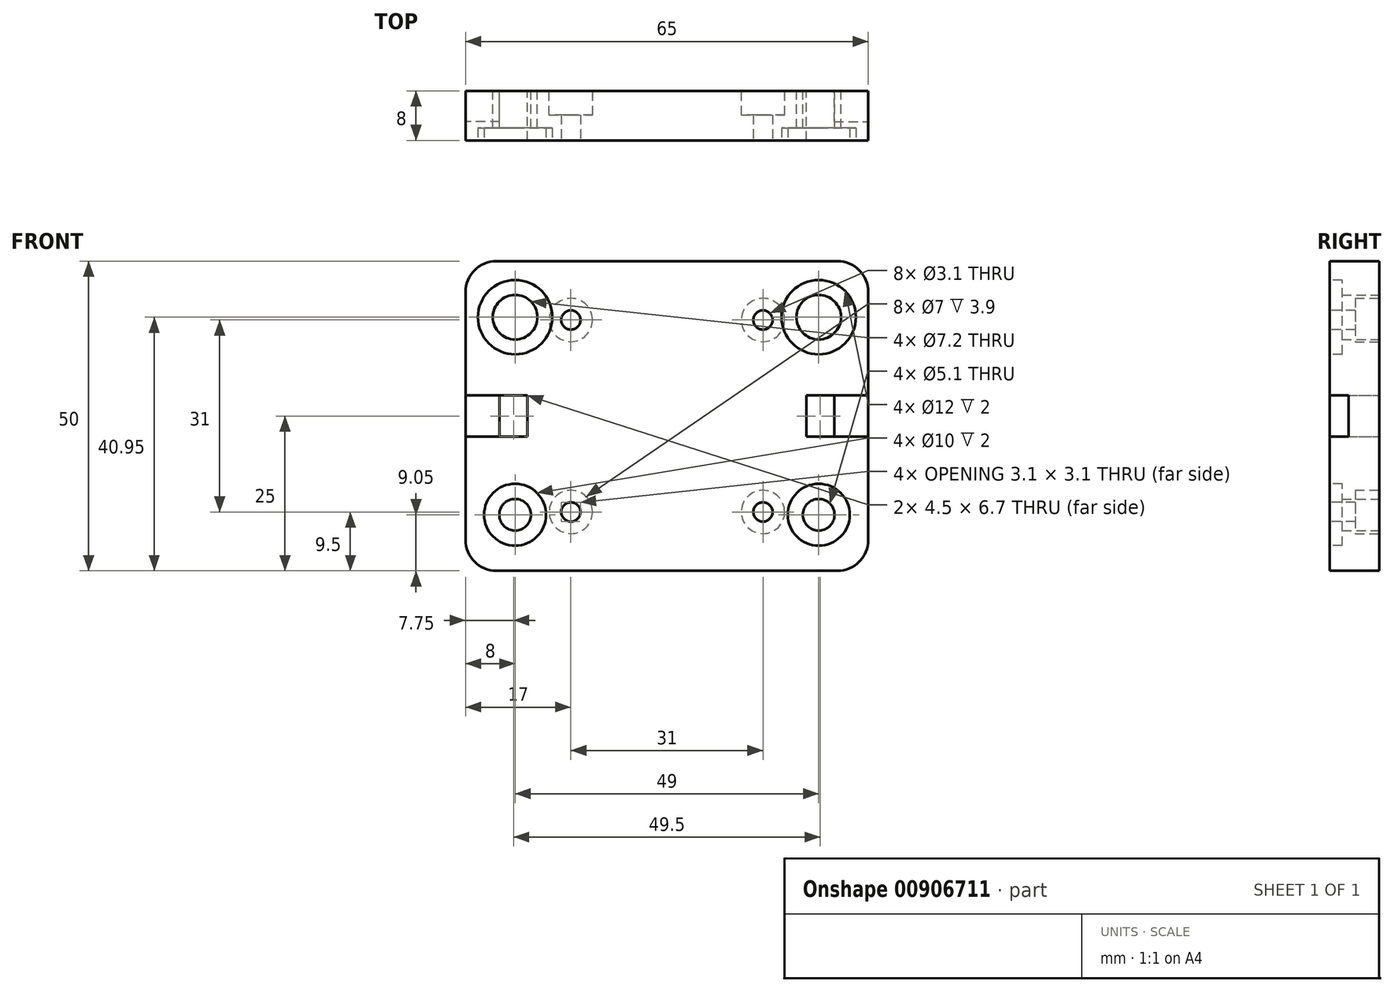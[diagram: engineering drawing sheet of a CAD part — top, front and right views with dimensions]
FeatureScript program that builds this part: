
annotation { "Feature Type Name" : "Feature", "Feature Type Description" : "" }
export const myFeature = defineFeature(function(context is Context, id is Id, definition is map)
    precondition{}
    {
        {
            var Q0;
            Q0=qCreatedBy(makeId("Front.planeOp"),FACE);
            var sketch = newSketch(context, id + "F0", { "sketchPlane" : qUnion([Q0])});
            skLineSegment(sketch, "E0.bottom", {"start": v(-32.5, 25) * mm, "end": v(32.5, 25) * mm});
            skLineSegment(sketch, "E0.top", {"start": v(-32.5, -25) * mm, "end": v(32.5, -25) * mm});
            skLineSegment(sketch, "E0.left", {"start": v(-32.5, 25) * mm, "end": v(-32.5, -25) * mm});
            skLineSegment(sketch, "E0.right", {"start": v(32.5, 25) * mm, "end": v(32.5, -25) * mm});
            skPoint(sketch, "E0.middle", {"position": v(0, 0) * mm});
            skLineSegment(sketch, "E1.bottom", {"start": v(-24.5, 15.95) * mm, "end": v(24.5, 15.95) * mm});
            skLineSegment(sketch, "E1.top", {"start": v(-24.5, -15.95) * mm, "end": v(24.5, -15.95) * mm});
            skLineSegment(sketch, "E1.left", {"start": v(-24.5, 15.95) * mm, "end": v(-24.5, -15.95) * mm});
            skLineSegment(sketch, "E1.right", {"start": v(24.5, 15.95) * mm, "end": v(24.5, -15.95) * mm});
            skCircle(sketch, "E2", {"center": v(-24.5, 15.95) * mm, "radius": 3.6 * mm});
            skCircle(sketch, "E3", {"center": v(24.5, 15.95) * mm, "radius": 3.6 * mm});
            skCircle(sketch, "E4", {"center": v(-24.5, -15.95) * mm, "radius": 2.55 * mm});
            skCircle(sketch, "E5", {"center": v(24.5, -15.95) * mm, "radius": 2.55 * mm});
            skLineSegment(sketch, "E6.bottom", {"start": v(-22.5, 3.35) * mm, "end": v(22.5, 3.35) * mm});
            skLineSegment(sketch, "E6.top", {"start": v(-22.5, -3.35) * mm, "end": v(22.5, -3.35) * mm});
            skLineSegment(sketch, "E6.left", {"start": v(-22.5, 3.35) * mm, "end": v(-22.5, -3.35) * mm});
            skLineSegment(sketch, "E6.right", {"start": v(22.5, 3.35) * mm, "end": v(22.5, -3.35) * mm});
            skLineSegment(sketch, "E7.bottom", {"start": v(-27, 3.35) * mm, "end": v(27, 3.35) * mm});
            skLineSegment(sketch, "E7.top", {"start": v(-27, -3.35) * mm, "end": v(27, -3.35) * mm});
            skLineSegment(sketch, "E7.left", {"start": v(-27, 3.35) * mm, "end": v(-27, -3.35) * mm});
            skLineSegment(sketch, "E7.right", {"start": v(27, 3.35) * mm, "end": v(27, -3.35) * mm});
            skSolve(sketch);
        }
        {
            var Q0;
            Q0 = qSketchRegion(id + "F0", true);
            var Q1;
            {var subQ0=sQuery(id+"F0.wireOp",EDGE,"E2");var subQ1=sQuery(id+"F0.wireOp",EDGE,"E1.bottom");var subQ2=makeQuery(id+"F0.imprint","INTERSECT",VERTEX,{"derivedFrom":[subQ1,subQ0]});Q1=makeQuery(id+"F0.imprint","IMPRINT",FACE,{"disambiguationData":[TD([[makeQuery(id+"F0.imprint","IMPRINT",EDGE,{"disambiguationData":[TD([[subQ2,-1.0]])],"derivedFrom":subQ1}),-1.0]])]});}
            var Q2;
            {var subQ0=sQuery(id+"F0.wireOp",EDGE,"E4");var subQ1=sQuery(id+"F0.wireOp",EDGE,"E1.top");var subQ2=makeQuery(id+"F0.imprint","INTERSECT",VERTEX,{"derivedFrom":[subQ1,subQ0]});Q2=makeQuery(id+"F0.imprint","IMPRINT",FACE,{"disambiguationData":[TD([[makeQuery(id+"F0.imprint","IMPRINT",EDGE,{"disambiguationData":[TD([[subQ2,-1.0]])],"derivedFrom":subQ1}),1.0]])]});}
            var Q3;
            {var subQ5=sQuery(id+"F0.wireOp",EDGE,"E6.left");Q3=makeQuery(id+"F0.imprint","IMPRINT",FACE,{"disambiguationData":[TD([[makeQuery(id+"F0.imprint","IMPRINT",EDGE,{"derivedFrom":subQ5}),1.0]])]});}
            var Q4;
            {var subQ5=sQuery(id+"F0.wireOp",EDGE,"E6.right");Q4=makeQuery(id+"F0.imprint","IMPRINT",FACE,{"disambiguationData":[TD([[makeQuery(id+"F0.imprint","IMPRINT",EDGE,{"derivedFrom":subQ5}),-1.0]])]});}
            extrude(context, id + "F1", {"entities" : qUnion([Q0, Q1, Q2, Q3, Q4]), "depth" : 8 * mm, "offsetDistance" : 25 * mm});
        }
        {
            var Q0;
            Q0=makeQuery(id+"F1.opExtrude","CAP_FACE",FACE,{"disambiguationData":[OSD([sQuery(id+"F0.wireOp",EDGE,"E0.bottom"),sQuery(id+"F0.wireOp",EDGE,"E0.top"),sQuery(id+"F0.wireOp",EDGE,"E0.left"),sQuery(id+"F0.wireOp",EDGE,"E0.right"),sQuery(id+"F0.wireOp",EDGE,"E2"),sQuery(id+"F0.wireOp",EDGE,"E3"),sQuery(id+"F0.wireOp",EDGE,"E4"),sQuery(id+"F0.wireOp",EDGE,"E5"),sQuery(id+"F0.wireOp",EDGE,"E6.left"),sQuery(id+"F0.wireOp",EDGE,"E6.right"),sQuery(id+"F0.wireOp",EDGE,"E7.bottom"),sQuery(id+"F0.wireOp",EDGE,"E7.top"),sQuery(id+"F0.wireOp",EDGE,"E7.left"),sQuery(id+"F0.wireOp",EDGE,"E7.right")])],"isStart":false});
            var sketch = newSketch(context, id + "F2", { "sketchPlane" : qUnion([Q0])});
            skCircle(sketch, "E8", {"center": v(-24.5, 15.95) * mm, "radius": 6 * mm});
            skCircle(sketch, "E9", {"center": v(24.5, 15.95) * mm, "radius": 6 * mm});
            skCircle(sketch, "E10", {"center": v(-24.5, -15.95) * mm, "radius": 5 * mm});
            skCircle(sketch, "E11", {"center": v(24.5, -15.95) * mm, "radius": 5 * mm});
            skSolve(sketch);
        }
        {
            var Q0;
            Q0=makeQuery(id+"F2.imprint","IMPRINT",FACE,{"disambiguationData":[TD([[makeQuery(id+"F2.imprint","IMPRINT",EDGE,{"derivedFrom":sQuery(id+"F2.wireOp",EDGE,"E9")}),1.0]])]});
            var Q1;
            Q1=makeQuery(id+"F2.imprint","IMPRINT",FACE,{"disambiguationData":[TD([[makeQuery(id+"F2.imprint","IMPRINT",EDGE,{"derivedFrom":sQuery(id+"F2.wireOp",EDGE,"E8")}),1.0]])]});
            var Q2;
            Q2=makeQuery(id+"F2.imprint","IMPRINT",FACE,{"disambiguationData":[TD([[makeQuery(id+"F2.imprint","IMPRINT",EDGE,{"derivedFrom":sQuery(id+"F2.wireOp",EDGE,"E10")}),1.0]])]});
            var Q3;
            Q3=makeQuery(id+"F2.imprint","IMPRINT",FACE,{"disambiguationData":[TD([[makeQuery(id+"F2.imprint","IMPRINT",EDGE,{"derivedFrom":sQuery(id+"F2.wireOp",EDGE,"E11")}),1.0]])]});
            extrude(context, id + "F3", {"entities" : qUnion([Q0, Q1, Q2, Q3]), "operationType" : NewBodyOperationType.REMOVE, "oppositeDirection" : true, "depth" : 2 * mm, "offsetDistance" : 25 * mm});
        }
        {
            var Q0;
            Q0=makeQuery(id+"F1.opExtrude","CAP_FACE",FACE,{"disambiguationData":[OSD([sQuery(id+"F0.wireOp",EDGE,"E0.bottom"),sQuery(id+"F0.wireOp",EDGE,"E0.top"),sQuery(id+"F0.wireOp",EDGE,"E0.left"),sQuery(id+"F0.wireOp",EDGE,"E0.right"),sQuery(id+"F0.wireOp",EDGE,"E2"),sQuery(id+"F0.wireOp",EDGE,"E3"),sQuery(id+"F0.wireOp",EDGE,"E4"),sQuery(id+"F0.wireOp",EDGE,"E5"),sQuery(id+"F0.wireOp",EDGE,"E6.left"),sQuery(id+"F0.wireOp",EDGE,"E6.right"),sQuery(id+"F0.wireOp",EDGE,"E7.bottom"),sQuery(id+"F0.wireOp",EDGE,"E7.top"),sQuery(id+"F0.wireOp",EDGE,"E7.left"),sQuery(id+"F0.wireOp",EDGE,"E7.right")])],"isStart":false});
            var sketch = newSketch(context, id + "F4", { "sketchPlane" : qUnion([Q0])});
            skLineSegment(sketch, "E12.bottom", {"start": v(27, 3.35) * mm, "end": v(32.5, 3.35) * mm});
            skLineSegment(sketch, "E12.top", {"start": v(27, -3.35) * mm, "end": v(32.5, -3.35) * mm});
            skLineSegment(sketch, "E12.left", {"start": v(27, 3.35) * mm, "end": v(27, -3.35) * mm});
            skLineSegment(sketch, "E12.right", {"start": v(32.5, 3.35) * mm, "end": v(32.5, -3.35) * mm});
            skLineSegment(sketch, "E13.bottom", {"start": v(-27, 3.35) * mm, "end": v(-32.5, 3.35) * mm});
            skLineSegment(sketch, "E13.top", {"start": v(-27, -3.35) * mm, "end": v(-32.5, -3.35) * mm});
            skLineSegment(sketch, "E13.left", {"start": v(-27, 3.35) * mm, "end": v(-27, -3.35) * mm});
            skLineSegment(sketch, "E13.right", {"start": v(-32.5, 3.35) * mm, "end": v(-32.5, -3.35) * mm});
            skSolve(sketch);
        }
        {
            var Q0;
            Q0 = qSketchRegion(id + "F4", true);
            extrude(context, id + "F5", {"entities" : qUnion([Q0]), "operationType" : NewBodyOperationType.REMOVE, "oppositeDirection" : true, "depth" : 3 * mm, "offsetDistance" : 25 * mm});
        }
        {
            var Q0;
            Q0=makeQuery(id+"F1.opExtrude","CAP_FACE",FACE,{"disambiguationData":[OSD([sQuery(id+"F0.wireOp",EDGE,"E0.bottom"),sQuery(id+"F0.wireOp",EDGE,"E0.top"),sQuery(id+"F0.wireOp",EDGE,"E0.left"),sQuery(id+"F0.wireOp",EDGE,"E0.right"),sQuery(id+"F0.wireOp",EDGE,"E2"),sQuery(id+"F0.wireOp",EDGE,"E3"),sQuery(id+"F0.wireOp",EDGE,"E4"),sQuery(id+"F0.wireOp",EDGE,"E5"),sQuery(id+"F0.wireOp",EDGE,"E6.left"),sQuery(id+"F0.wireOp",EDGE,"E6.right"),sQuery(id+"F0.wireOp",EDGE,"E7.bottom"),sQuery(id+"F0.wireOp",EDGE,"E7.top"),sQuery(id+"F0.wireOp",EDGE,"E7.left"),sQuery(id+"F0.wireOp",EDGE,"E7.right")])],"isStart":false});
            var sketch = newSketch(context, id + "F6", { "sketchPlane" : qUnion([Q0])});
            skLineSegment(sketch, "E14.bottom", {"start": v(-15.5, 15.5) * mm, "end": v(15.5, 15.5) * mm});
            skLineSegment(sketch, "E14.top", {"start": v(-15.5, -15.5) * mm, "end": v(15.5, -15.5) * mm});
            skLineSegment(sketch, "E14.left", {"start": v(-15.5, 15.5) * mm, "end": v(-15.5, -15.5) * mm});
            skLineSegment(sketch, "E14.right", {"start": v(15.5, 15.5) * mm, "end": v(15.5, -15.5) * mm});
            skPoint(sketch, "E14.middle", {"position": v(0, 0) * mm});
            skCircle(sketch, "E15", {"center": v(-15.5, 15.5) * mm, "radius": 1.55 * mm});
            skCircle(sketch, "E16", {"center": v(15.5, 15.5) * mm, "radius": 1.55 * mm});
            skCircle(sketch, "E17", {"center": v(-15.5, -15.5) * mm, "radius": 1.55 * mm});
            skCircle(sketch, "E18", {"center": v(15.5, -15.5) * mm, "radius": 1.55 * mm});
            skLineSegment(sketch, "E19", {"start": v(-15.5, 15.5) * mm, "end": v(-15.5, 25) * mm});
            skSolve(sketch);
        }
        {
            var Q0;
            {var subQ0=sQuery(id+"F6.wireOp",EDGE,"E14.left");var subQ1=sQuery(id+"F6.wireOp",EDGE,"E14.bottom");var subQ2=makeQuery(id+"F6.imprint","INTERSECT",VERTEX,{"derivedFrom":[subQ1,subQ0]});Q0=makeQuery(id+"F6.imprint","IMPRINT",FACE,{"disambiguationData":[TD([[makeQuery(id+"F6.imprint","IMPRINT",EDGE,{"disambiguationData":[TD([[subQ2,-1.0]])],"derivedFrom":subQ1}),1.0]])]});}
            var Q1;
            {var subQ0=sQuery(id+"F6.wireOp",EDGE,"E14.left");var subQ1=sQuery(id+"F6.wireOp",EDGE,"E14.bottom");var subQ2=makeQuery(id+"F6.imprint","INTERSECT",VERTEX,{"derivedFrom":[subQ1,subQ0]});Q1=makeQuery(id+"F6.imprint","IMPRINT",FACE,{"disambiguationData":[TD([[makeQuery(id+"F6.imprint","IMPRINT",EDGE,{"disambiguationData":[TD([[subQ2,-1.0]])],"derivedFrom":subQ1}),-1.0]])]});}
            var Q2;
            {var subQ0=sQuery(id+"F6.wireOp",EDGE,"E14.right");var subQ1=sQuery(id+"F6.wireOp",EDGE,"E14.bottom");var subQ2=makeQuery(id+"F6.imprint","INTERSECT",VERTEX,{"derivedFrom":[subQ1,subQ0]});Q2=makeQuery(id+"F6.imprint","IMPRINT",FACE,{"disambiguationData":[TD([[makeQuery(id+"F6.imprint","IMPRINT",EDGE,{"disambiguationData":[TD([[subQ2,1.0]])],"derivedFrom":subQ1}),1.0]])]});}
            var Q3;
            {var subQ0=sQuery(id+"F6.wireOp",EDGE,"E14.right");var subQ1=sQuery(id+"F6.wireOp",EDGE,"E14.bottom");var subQ2=makeQuery(id+"F6.imprint","INTERSECT",VERTEX,{"derivedFrom":[subQ1,subQ0]});Q3=makeQuery(id+"F6.imprint","IMPRINT",FACE,{"disambiguationData":[TD([[makeQuery(id+"F6.imprint","IMPRINT",EDGE,{"disambiguationData":[TD([[subQ2,1.0]])],"derivedFrom":subQ1}),-1.0]])]});}
            var Q4;
            {var subQ0=sQuery(id+"F6.wireOp",EDGE,"E14.left");var subQ1=sQuery(id+"F6.wireOp",EDGE,"E14.top");var subQ2=makeQuery(id+"F6.imprint","INTERSECT",VERTEX,{"derivedFrom":[subQ1,subQ0]});Q4=makeQuery(id+"F6.imprint","IMPRINT",FACE,{"disambiguationData":[TD([[makeQuery(id+"F6.imprint","IMPRINT",EDGE,{"disambiguationData":[TD([[subQ2,-1.0]])],"derivedFrom":subQ1}),-1.0]])]});}
            var Q5;
            {var subQ0=sQuery(id+"F6.wireOp",EDGE,"E14.left");var subQ1=sQuery(id+"F6.wireOp",EDGE,"E14.top");var subQ2=makeQuery(id+"F6.imprint","INTERSECT",VERTEX,{"derivedFrom":[subQ1,subQ0]});Q5=makeQuery(id+"F6.imprint","IMPRINT",FACE,{"disambiguationData":[TD([[makeQuery(id+"F6.imprint","IMPRINT",EDGE,{"disambiguationData":[TD([[subQ2,-1.0]])],"derivedFrom":subQ1}),1.0]])]});}
            var Q6;
            {var subQ0=sQuery(id+"F6.wireOp",EDGE,"E14.right");var subQ1=sQuery(id+"F6.wireOp",EDGE,"E14.top");var subQ2=makeQuery(id+"F6.imprint","INTERSECT",VERTEX,{"derivedFrom":[subQ1,subQ0]});Q6=makeQuery(id+"F6.imprint","IMPRINT",FACE,{"disambiguationData":[TD([[makeQuery(id+"F6.imprint","IMPRINT",EDGE,{"disambiguationData":[TD([[subQ2,1.0]])],"derivedFrom":subQ1}),1.0]])]});}
            var Q7;
            {var subQ0=sQuery(id+"F6.wireOp",EDGE,"E14.right");var subQ1=sQuery(id+"F6.wireOp",EDGE,"E14.top");var subQ2=makeQuery(id+"F6.imprint","INTERSECT",VERTEX,{"derivedFrom":[subQ1,subQ0]});Q7=makeQuery(id+"F6.imprint","IMPRINT",FACE,{"disambiguationData":[TD([[makeQuery(id+"F6.imprint","IMPRINT",EDGE,{"disambiguationData":[TD([[subQ2,1.0]])],"derivedFrom":subQ1}),-1.0]])]});}
            var Q8;
            {var subQ0=sQuery(id+"F6.wireOp",EDGE,"E19");var subQ3=sQuery(id+"F6.wireOp",EDGE,"E15");var subQ5=makeQuery(id+"F6.imprint","INTERSECT",VERTEX,{"derivedFrom":[subQ3,subQ0]});Q8=makeQuery(id+"F6.imprint","IMPRINT",FACE,{"disambiguationData":[TD([[makeQuery(id+"F6.imprint","IMPRINT",EDGE,{"disambiguationData":[TD([[subQ5,-1.0]])],"derivedFrom":subQ3}),1.0]])]});}
            extrude(context, id + "F7", {"entities" : qUnion([Q0, Q1, Q2, Q3, Q4, Q5, Q6, Q7, Q8]), "operationType" : NewBodyOperationType.REMOVE, "oppositeDirection" : true, "depth" : 7 * mm, "offsetDistance" : 25 * mm});
        }
        {
            var Q0;
            Q0=makeQuery(id+"F1.opExtrude","CAP_FACE",FACE,{"disambiguationData":[OSD([sQuery(id+"F0.wireOp",EDGE,"E0.bottom"),sQuery(id+"F0.wireOp",EDGE,"E0.top"),sQuery(id+"F0.wireOp",EDGE,"E0.left"),sQuery(id+"F0.wireOp",EDGE,"E0.right"),sQuery(id+"F0.wireOp",EDGE,"E2"),sQuery(id+"F0.wireOp",EDGE,"E3"),sQuery(id+"F0.wireOp",EDGE,"E4"),sQuery(id+"F0.wireOp",EDGE,"E5"),sQuery(id+"F0.wireOp",EDGE,"E6.left"),sQuery(id+"F0.wireOp",EDGE,"E6.right"),sQuery(id+"F0.wireOp",EDGE,"E7.bottom"),sQuery(id+"F0.wireOp",EDGE,"E7.top"),sQuery(id+"F0.wireOp",EDGE,"E7.left"),sQuery(id+"F0.wireOp",EDGE,"E7.right")])],"isStart":true});
            var sketch = newSketch(context, id + "F8", { "sketchPlane" : qUnion([Q0])});
            skCircle(sketch, "E20", {"center": v(-15.5, 15.5) * mm, "radius": 3.5 * mm});
            skCircle(sketch, "E21", {"center": v(15.5, 15.5) * mm, "radius": 3.5 * mm});
            skCircle(sketch, "E22", {"center": v(15.5, -15.5) * mm, "radius": 3.5 * mm});
            skCircle(sketch, "E23", {"center": v(-15.5, -15.5) * mm, "radius": 3.5 * mm});
            skSolve(sketch);
        }
        {
            var Q0;
            Q0=makeQuery(id+"F8.imprint","IMPRINT",FACE,{"disambiguationData":[TD([[makeQuery(id+"F8.imprint","IMPRINT",EDGE,{"derivedFrom":sQuery(id+"F8.wireOp",EDGE,"E20")}),1.0]])]});
            var Q1;
            Q1=makeQuery(id+"F8.imprint","IMPRINT",FACE,{"disambiguationData":[TD([[makeQuery(id+"F8.imprint","IMPRINT",EDGE,{"derivedFrom":sQuery(id+"F8.wireOp",EDGE,"E23")}),1.0]])]});
            var Q2;
            Q2=makeQuery(id+"F8.imprint","IMPRINT",FACE,{"disambiguationData":[TD([[makeQuery(id+"F8.imprint","IMPRINT",EDGE,{"derivedFrom":sQuery(id+"F8.wireOp",EDGE,"E21")}),1.0]])]});
            var Q3;
            Q3=makeQuery(id+"F8.imprint","IMPRINT",FACE,{"disambiguationData":[TD([[makeQuery(id+"F8.imprint","IMPRINT",EDGE,{"derivedFrom":sQuery(id+"F8.wireOp",EDGE,"E22")}),1.0]])]});
            extrude(context, id + "F9", {"entities" : qUnion([Q0, Q1, Q2, Q3]), "operationType" : NewBodyOperationType.REMOVE, "oppositeDirection" : true, "depth" : 3.9 * mm, "offsetDistance" : 25 * mm});
        }
        {
            var Q0;
            Q0=makeQuery(id+"F1.opExtrude","SWEPT_EDGE",EDGE,{"disambiguationData":[OSD([sQuery(id+"F0.wireOp",EDGE,"E0.bottom"),sQuery(id+"F0.wireOp",EDGE,"E0.right")])]});
            var Q1;
            Q1=makeQuery(id+"F1.opExtrude","SWEPT_EDGE",EDGE,{"disambiguationData":[OSD([sQuery(id+"F0.wireOp",EDGE,"E0.top"),sQuery(id+"F0.wireOp",EDGE,"E0.right")])]});
            var Q2;
            Q2=makeQuery(id+"F1.opExtrude","SWEPT_EDGE",EDGE,{"disambiguationData":[OSD([sQuery(id+"F0.wireOp",EDGE,"E0.bottom"),sQuery(id+"F0.wireOp",EDGE,"E0.left")])]});
            var Q3;
            Q3=makeQuery(id+"F1.opExtrude","SWEPT_EDGE",EDGE,{"disambiguationData":[OSD([sQuery(id+"F0.wireOp",EDGE,"E0.top"),sQuery(id+"F0.wireOp",EDGE,"E0.left")])]});
            fillet(context, id + "F10", {"entities" : qUnion([Q0, Q1, Q2, Q3]), "radius" : 5 * mm, "tangentPropagation" : true, "allowEdgeOverflow" : false});
        }
    });
